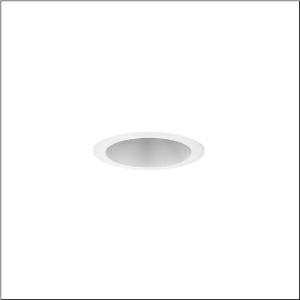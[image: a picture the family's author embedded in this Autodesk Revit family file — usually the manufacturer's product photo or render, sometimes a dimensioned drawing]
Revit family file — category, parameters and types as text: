
# Revit family: lunis_31_mini_51dn16de31
name_source: partatom
category: Lighting Fixtures
units: mm (PartAtom-declared; Revit-internal decimal feet)

## family parameters
Cut with Voids When Loaded = No
Host = Face
Light Source = No
Part Type = Normal
Room Calculation Point = No
Round Connector Dimension = Use Diameter
Shared = No

## types (1)
- Lunis 31 mini (1 x LED, 1000 lm, 8.3 W, 3000K)
    Apparent Load = 8 VA
    CIE Flux Codes = 69 93 99 100 100
    Color Rendering = 80
    Color Temperature = 3000K
    Default Elevation = 1800 mm
    Description = Lunis 31 mini, downlight, light control with reflector, light emission: direct distribution, LED rated luminous flux: 1.000lm, light colour: 830, mains connection: 220..240V, AC, 50/60Hz, housing, white, protection rating (complete): IP20, protection rating (on room side): IP54, insulation class (complete): insulation class II (safety insulation), certification: CE, packaging unit: 1 piece
    Height = 0 mm  [stored 0 ft]
    Lamp = 1 x LED
    Lamp Light Flux = 1000 lm
    Lamp Power = 8.3 W
    Lamp count = 1
    Length = 188 mm  [stored 0.616798 ft]
    Luminous efficacy = 120 lm/W
    Manufacturer = Siteco
    ModVariant = No
    Model = 51DN16DE31
    Mounting Place = Ceiling
    Mounting Type = Recessed
    Number of Poles = 1
    OnlyDefault = Yes
    Power Factor = 1
    Product Name = Lunis 31 mini
    Product group = downlight
    ProductGroupID = 401
    Protection Class = Protection class II
    Protection Degree = IP 20
    RLX_Detail_Level = 1
    RLX_Emergency_Light_Flux = 0 lm
    RLX_Emergency_Type = 0
    RLX_Emergency_Type_DB = No
    RlxData = <blob elided: 21761 chars, md5=76c28e90>
    Socket = socket
    Standby Power = 0 W
    System Light Flux = 1000 lm
    System Power = 8 W
    Type Comments = Product without accessories
    Type Image = l_1345911.jpg
    URL = http://relux.com
    VarID = ---
    Voltage = 0 V
    Weight = 0.00 kg
    Width = 0 mm  [stored 0 ft]

note: [stored X ft] marks values corroborated as IEEE doubles in the binary element streams (Revit-internal decimal feet)

## geometry (parser evidence)
native form markers: Blend x4, Sweep x12
no freeform markers — native parametric forms only
